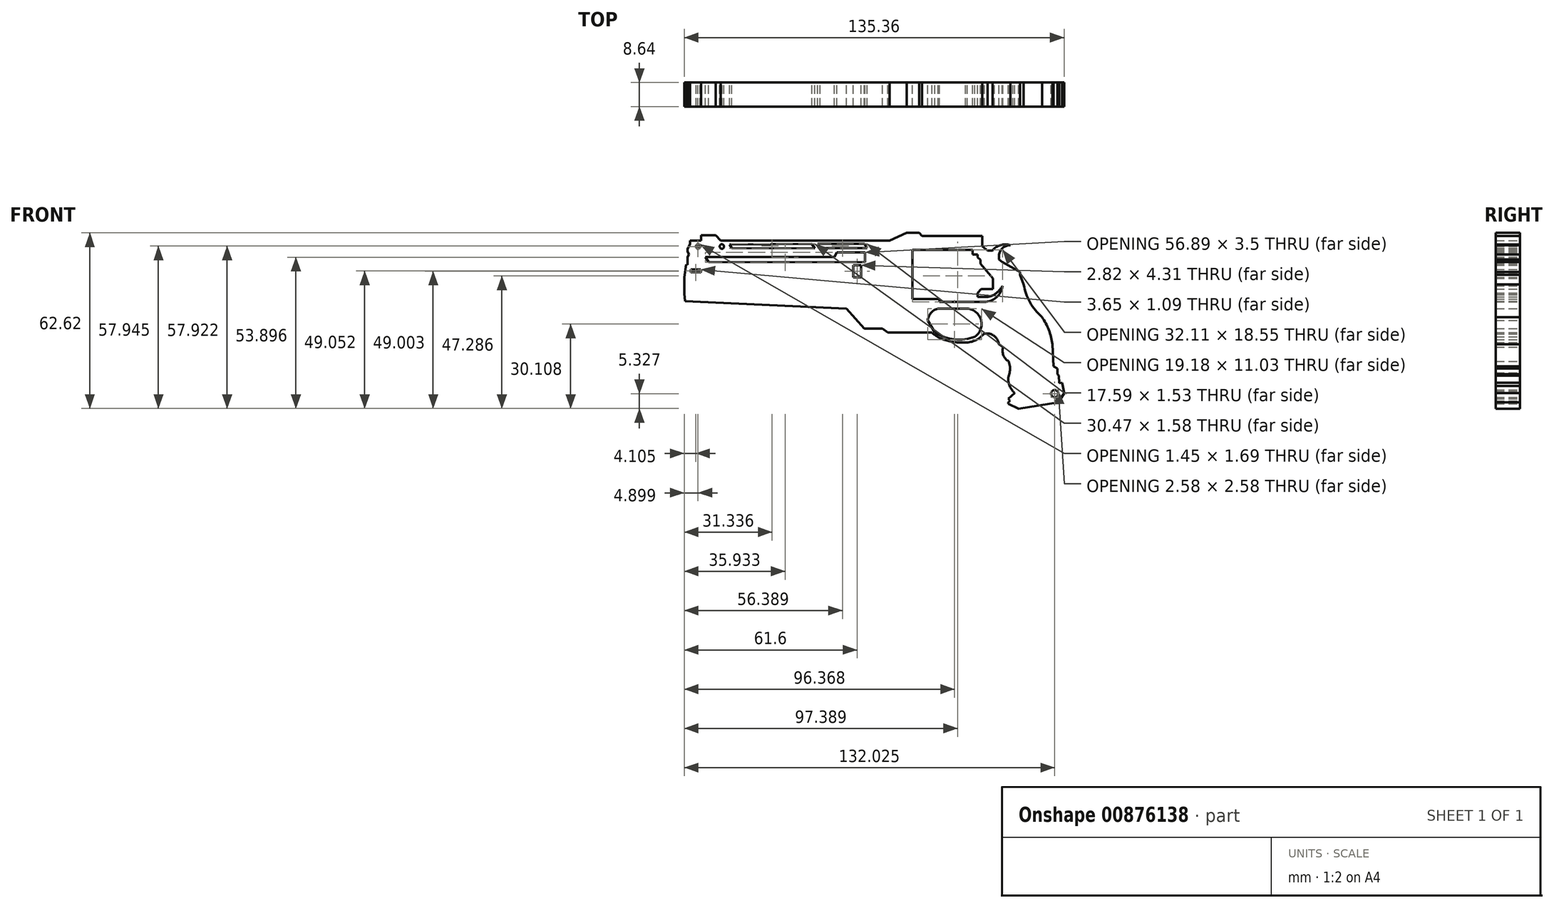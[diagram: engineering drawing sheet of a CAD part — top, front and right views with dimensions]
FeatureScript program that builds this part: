
annotation { "Feature Type Name" : "Feature", "Feature Type Description" : "" }
export const myFeature = defineFeature(function(context is Context, id is Id, definition is map)
    precondition{}
    {
        {
            var Q0;
            Q0=qCreatedBy(makeId("Front.planeOp"),FACE);
            var sketch = newSketch(context, id + "F0", { "sketchPlane" : qUnion([Q0])});
            skLineSegment(sketch, "E0", {"start": v(-67.89, 8.33) * mm, "end": v(-67.89, 14.23) * mm});
            skLineSegment(sketch, "E1", {"start": v(-67.89, 14.23) * mm, "end": v(-67.27, 18.7) * mm});
            skLineSegment(sketch, "E2", {"start": v(-67.27, 18.7) * mm, "end": v(-66.73, 18.63) * mm});
            skLineSegment(sketch, "E3", {"start": v(-66.73, 18.63) * mm, "end": v(-66.73, 21.38) * mm});
            skLineSegment(sketch, "E4", {"start": v(-66.73, 21.38) * mm, "end": v(-66.2, 22.3) * mm});
            skLineSegment(sketch, "E5", {"start": v(-66.2, 22.3) * mm, "end": v(-66.73, 23.47) * mm});
            skLineSegment(sketch, "E6", {"start": v(-66.73, 23.47) * mm, "end": v(-66.73, 24.31) * mm});
            skLineSegment(sketch, "E7", {"start": v(-66.73, 24.31) * mm, "end": v(-65.84, 25.94) * mm});
            skLineSegment(sketch, "E8", {"start": v(-65.84, 25.94) * mm, "end": v(-65.84, 27.21) * mm});
            skLineSegment(sketch, "E9", {"start": v(-65.84, 27.21) * mm, "end": v(5.25, 27.21) * mm});
            skLineSegment(sketch, "E10", {"start": v(5.25, 27.21) * mm, "end": v(11.39, 30) * mm});
            skLineSegment(sketch, "E11", {"start": v(11.39, 30) * mm, "end": v(15.19, 30) * mm});
            skLineSegment(sketch, "E12", {"start": v(15.19, 30) * mm, "end": v(15.88, 30) * mm});
            skLineSegment(sketch, "E13", {"start": v(15.88, 30) * mm, "end": v(16.87, 28.96) * mm});
            skLineSegment(sketch, "E14", {"start": v(16.87, 28.96) * mm, "end": v(38.33, 28.96) * mm});
            skLineSegment(sketch, "E15", {"start": v(38.33, 28.96) * mm, "end": v(38.33, 19.68) * mm});
            skLineSegment(sketch, "E16", {"start": v(38.33, 19.68) * mm, "end": v(40.93, 18) * mm});
            skLineSegment(sketch, "E17", {"start": v(40.93, 18) * mm, "end": v(42.2, 18) * mm});
            skLineSegment(sketch, "E18", {"start": v(42.2, 18) * mm, "end": v(45.38, 19.68) * mm});
            skLineSegment(sketch, "E19", {"start": v(45.38, 19.68) * mm, "end": v(38.33, 25.17) * mm});
            skLineSegment(sketch, "E20", {"start": v(45.38, 19.68) * mm, "end": v(51.8, 16.04) * mm});
            skLineSegment(sketch, "E21", {"start": v(51.8, 16.04) * mm, "end": v(51.8, 15.12) * mm});
            skLineSegment(sketch, "E22", {"start": v(51.8, 15.12) * mm, "end": v(46.94, 15.12) * mm});
            skArc(sketch, "E23", {"start": v(46.94, 15.12) * mm, "mid": v(45.8, 16.55) * mm, "end": v(44.1, 17.21) * mm});
            skArc(sketch, "E24", {"start": v(42.64, 8) * mm, "mid": v(45.55, 11.1) * mm, "end": v(46.94, 15.12) * mm});
            skArc(sketch, "E25", {"start": v(39.02, 7.14) * mm, "mid": v(40.89, 7.34) * mm, "end": v(42.64, 8) * mm});
            skLineSegment(sketch, "E26", {"start": v(39.02, 7.14) * mm, "end": v(23.08, 7.14) * mm});
            skLineSegment(sketch, "E27", {"start": v(23.08, 7.14) * mm, "end": v(23.08, 5.4) * mm});
            skLineSegment(sketch, "E28", {"start": v(23.08, 5.4) * mm, "end": v(39.02, 5.4) * mm});
            skArc(sketch, "E29", {"start": v(39.02, 5.4) * mm, "mid": v(43.36, 7.02) * mm, "end": v(45.55, 11.1) * mm});
            skArc(sketch, "E30", {"start": v(22.56, 3) * mm, "mid": v(20.04, 1.48) * mm, "end": v(18.89, -1.23) * mm});
            skArc(sketch, "E31", {"start": v(35.67, -7.02) * mm, "mid": v(37.89, -1.05) * mm, "end": v(32.98, 3) * mm});
            skArc(sketch, "E32", {"start": v(21.47, -5.51) * mm, "mid": v(28.4, -7.94) * mm, "end": v(35.67, -7.02) * mm});
            skLineSegment(sketch, "E33", {"start": v(21.47, -5.51) * mm, "end": v(18.89, -1.23) * mm});
            skLineSegment(sketch, "E34", {"start": v(22.56, 3) * mm, "end": v(32.98, 3) * mm});
            skArc(sketch, "E35", {"start": v(32.33, -9.05) * mm, "mid": v(35.94, -8.28) * mm, "end": v(38.85, -6) * mm});
            skArc(sketch, "E36", {"start": v(24.52, -8) * mm, "mid": v(28.37, -8.94) * mm, "end": v(32.33, -9.05) * mm});
            skArc(sketch, "E37", {"start": v(18, -2.7) * mm, "mid": v(20.82, -5.9) * mm, "end": v(24.52, -8) * mm});
            skArc(sketch, "E38", {"start": v(44.24, -9.7) * mm, "mid": v(42.4, -6.6) * mm, "end": v(38.85, -6) * mm});
            skLineSegment(sketch, "E39", {"start": v(44.24, -9.7) * mm, "end": v(45.72, -10.7) * mm});
            skArc(sketch, "E40", {"start": v(45.72, -10.7) * mm, "mid": v(45.85, -13.6) * mm, "end": v(47.73, -15.8) * mm});
            skArc(sketch, "E41", {"start": v(48.08, -19.87) * mm, "mid": v(48.19, -17.8) * mm, "end": v(47.73, -15.8) * mm});
            skArc(sketch, "E42", {"start": v(48.08, -19.87) * mm, "mid": v(47.7, -23.34) * mm, "end": v(49.28, -26.44) * mm});
            skArc(sketch, "E43", {"start": v(49.28, -26.44) * mm, "mid": v(49.57, -26.8) * mm, "end": v(49.9, -27.11) * mm});
            skLineSegment(sketch, "E44", {"start": v(49.9, -27.11) * mm, "end": v(47.57, -29.1) * mm});
            skLineSegment(sketch, "E45", {"start": v(47.57, -29.1) * mm, "end": v(48.2, -29.84) * mm});
            skLineSegment(sketch, "E46", {"start": v(48.2, -29.84) * mm, "end": v(47.57, -30.38) * mm});
            skLineSegment(sketch, "E47", {"start": v(47.57, -30.38) * mm, "end": v(47.57, -30.87) * mm});
            skLineSegment(sketch, "E48", {"start": v(47.57, -30.87) * mm, "end": v(51.25, -32.62) * mm});
            skLineSegment(sketch, "E49", {"start": v(51.25, -32.62) * mm, "end": v(65.5, -30.38) * mm});
            skLineSegment(sketch, "E50", {"start": v(65.5, -30.38) * mm, "end": v(67.47, -27.11) * mm});
            skLineSegment(sketch, "E51", {"start": v(67.47, -27.11) * mm, "end": v(66.96, -24.58) * mm});
            skLineSegment(sketch, "E52", {"start": v(66.96, -24.58) * mm, "end": v(61.97, -25.57) * mm});
            skLineSegment(sketch, "E53", {"start": v(61.97, -25.57) * mm, "end": v(60.63, -27.68) * mm});
            skLineSegment(sketch, "E54", {"start": v(60.63, -27.68) * mm, "end": v(47.57, -30.38) * mm});
            skLineSegment(sketch, "E55", {"start": v(49.9, -27.11) * mm, "end": v(63.92, -23.25) * mm});
            skArc(sketch, "E56", {"start": v(53.08, 11.64) * mm, "mid": v(55.33, 5.26) * mm, "end": v(59.59, 0) * mm});
            skArc(sketch, "E57", {"start": v(63.3, -9.75) * mm, "mid": v(62.05, -4.64) * mm, "end": v(59.59, 0) * mm});
            skLineSegment(sketch, "E58", {"start": v(63.3, -9.75) * mm, "end": v(63.92, -23.25) * mm});
            skLineSegment(sketch, "E59", {"start": v(63.67, -17.63) * mm, "end": v(65.1, -18.36) * mm});
            skLineSegment(sketch, "E60", {"start": v(65.1, -18.36) * mm, "end": v(65.18, -20.34) * mm});
            skLineSegment(sketch, "E61", {"start": v(65.18, -20.34) * mm, "end": v(65.67, -20.82) * mm});
            skLineSegment(sketch, "E62", {"start": v(65.67, -20.82) * mm, "end": v(65.79, -23.5) * mm});
            skLineSegment(sketch, "E63", {"start": v(65.79, -23.5) * mm, "end": v(66.77, -23.46) * mm});
            skLineSegment(sketch, "E64", {"start": v(66.77, -23.46) * mm, "end": v(66.96, -24.58) * mm});
            skLineSegment(sketch, "E65", {"start": v(53.08, 11.64) * mm, "end": v(51.8, 15.12) * mm});
            skLineSegment(sketch, "E66", {"start": v(42.34, 0) * mm, "end": v(50.31, 8.3) * mm});
            skLineSegment(sketch, "E67", {"start": v(50.31, 8.3) * mm, "end": v(51.56, 13.38) * mm});
            skPoint(sketch, "E67.endSnap0", {"position": v(52.44, 13.38) * mm});
            skLineSegment(sketch, "E68", {"start": v(42.34, 0) * mm, "end": v(43.97, -1.57) * mm});
            skLineSegment(sketch, "E69", {"start": v(43.97, -1.57) * mm, "end": v(52.1, 6.9) * mm});
            skLineSegment(sketch, "E70", {"start": v(52.1, 6.9) * mm, "end": v(53.08, 11.64) * mm});
            skLineSegment(sketch, "E71", {"start": v(20.37, -5.51) * mm, "end": v(4.66, -5.51) * mm});
            skLineSegment(sketch, "E72", {"start": v(4.66, -5.51) * mm, "end": v(2.8, -4.12) * mm});
            skLineSegment(sketch, "E73", {"start": v(2.8, -4.12) * mm, "end": v(15, -4.12) * mm});
            skLineSegment(sketch, "E74", {"start": v(2.8, -4.12) * mm, "end": v(-3.73, -4.12) * mm});
            skLineSegment(sketch, "E75", {"start": v(-3.73, -4.12) * mm, "end": v(-10.07, 2.98) * mm});
            skLineSegment(sketch, "E76", {"start": v(-10.07, 2.98) * mm, "end": v(-67.6, 5.7) * mm});
            skLineSegment(sketch, "E77", {"start": v(-67.6, 5.7) * mm, "end": v(-67.89, 8.33) * mm});
            skLineSegment(sketch, "E78", {"start": v(-8.15, 8.33) * mm, "end": v(-67.89, 8.33) * mm});
            skLineSegment(sketch, "E79", {"start": v(-67.89, 14.23) * mm, "end": v(-7.7, 14.23) * mm});
            skLineSegment(sketch, "E80", {"start": v(-7.7, 14.23) * mm, "end": v(-7.7, 18.54) * mm});
            skLineSegment(sketch, "E81", {"start": v(-7.7, 18.54) * mm, "end": v(-66.73, 18.63) * mm});
            skLineSegment(sketch, "E82", {"start": v(-66.73, 21.38) * mm, "end": v(-14.4, 21.38) * mm});
            skLineSegment(sketch, "E83", {"start": v(-14.4, 21.38) * mm, "end": v(-13.48, 23.03) * mm});
            skLineSegment(sketch, "E84", {"start": v(-13.48, 23.03) * mm, "end": v(-3.51, 23.03) * mm});
            skLineSegment(sketch, "E85", {"start": v(-3.51, 23.03) * mm, "end": v(-3.51, 19.53) * mm});
            skLineSegment(sketch, "E86", {"start": v(-3.51, 19.53) * mm, "end": v(-59.21, 19.61) * mm});
            skLineSegment(sketch, "E87", {"start": v(-59.21, 19.61) * mm, "end": v(-60.4, 21.38) * mm});
            skLineSegment(sketch, "E88", {"start": v(7.79, 16.11) * mm, "end": v(7.79, 8.33) * mm});
            skLineSegment(sketch, "E89", {"start": v(15.1, 6.47) * mm, "end": v(23.08, 6.47) * mm});
            skLineSegment(sketch, "E90", {"start": v(15.1, 6.47) * mm, "end": v(13.45, 6.47) * mm});
            skLineSegment(sketch, "E91", {"start": v(13.45, 6.47) * mm, "end": v(13.45, 23.94) * mm});
            skLineSegment(sketch, "E92", {"start": v(13.45, 23.94) * mm, "end": v(34.92, 23.94) * mm});
            skLineSegment(sketch, "E93", {"start": v(34.92, 23.94) * mm, "end": v(34.92, 7.14) * mm});
            skLineSegment(sketch, "E94", {"start": v(34.92, 22.36) * mm, "end": v(36.64, 22.36) * mm});
            skLineSegment(sketch, "E95", {"start": v(36.64, 22.36) * mm, "end": v(36.64, 21.3) * mm});
            skLineSegment(sketch, "E96", {"start": v(36.64, 21.3) * mm, "end": v(37.66, 20.43) * mm});
            skLineSegment(sketch, "E97", {"start": v(37.66, 20.43) * mm, "end": v(37.66, 13.86) * mm});
            skLineSegment(sketch, "E98", {"start": v(37.66, 13.86) * mm, "end": v(42.07, 13.86) * mm});
            skLineSegment(sketch, "E99", {"start": v(42.07, 13.86) * mm, "end": v(42.07, 10) * mm});
            skLineSegment(sketch, "E100", {"start": v(42.07, 10) * mm, "end": v(37.93, 10) * mm});
            skLineSegment(sketch, "E101", {"start": v(37.93, 10) * mm, "end": v(36.64, 8.65) * mm});
            skLineSegment(sketch, "E102", {"start": v(36.64, 8.65) * mm, "end": v(36.64, 7.14) * mm});
            skLineSegment(sketch, "E103", {"start": v(11.2, 7.8) * mm, "end": v(11.18, 7.8) * mm});
            skLineSegment(sketch, "E104", {"start": v(-7.7, 14.23) * mm, "end": v(-7.7, 8.33) * mm});
            skLineSegment(sketch, "E105", {"start": v(-7.7, 8.33) * mm, "end": v(7.79, 8.33) * mm});
            skLineSegment(sketch, "E106", {"start": v(-7.7, 14.23) * mm, "end": v(4.44, 14.23) * mm});
            skLineSegment(sketch, "E107", {"start": v(4.23, 16.11) * mm, "end": v(4.44, 16.11) * mm});
            skLineSegment(sketch, "E108", {"start": v(-4.88, 14.23) * mm, "end": v(-4.88, 18.48) * mm});
            skLineSegment(sketch, "E109", {"start": v(-4.88, 18.48) * mm, "end": v(-7.7, 18.54) * mm});
            skLineSegment(sketch, "E110", {"start": v(7.79, 18.62) * mm, "end": v(-7.7, 18.54) * mm});
            skLineSegment(sketch, "E111", {"start": v(7.79, 18.62) * mm, "end": v(13.45, 18.62) * mm});
            skLineSegment(sketch, "E112", {"start": v(-3.51, 23.03) * mm, "end": v(2.61, 23.03) * mm});
            skLineSegment(sketch, "E113", {"start": v(2.61, 23.03) * mm, "end": v(3.29, 22.46) * mm});
            skLineSegment(sketch, "E114", {"start": v(3.29, 22.46) * mm, "end": v(10.44, 22.46) * mm});
            skLineSegment(sketch, "E115", {"start": v(10.44, 22.46) * mm, "end": v(11.86, 24.01) * mm});
            skLineSegment(sketch, "E116", {"start": v(11.86, 24.01) * mm, "end": v(13.45, 23.94) * mm});
            skLineSegment(sketch, "E117", {"start": v(37.66, 18.98) * mm, "end": v(42.07, 13.86) * mm});
            skLineSegment(sketch, "E118", {"start": v(37.66, 15.97) * mm, "end": v(39.87, 13.86) * mm});
            skLineSegment(sketch, "E119", {"start": v(13.45, 11.6) * mm, "end": v(34.92, 11.6) * mm});
            skLineSegment(sketch, "E120", {"start": v(13.45, 20.43) * mm, "end": v(34.92, 20.43) * mm});
            skLineSegment(sketch, "E121", {"start": v(-66.2, 22.3) * mm, "end": v(-17.8, 22.3) * mm});
            skLineSegment(sketch, "E122", {"start": v(-17.8, 22.3) * mm, "end": v(-17.18, 23.2) * mm});
            skLineSegment(sketch, "E123", {"start": v(-17.18, 23.2) * mm, "end": v(2.58, 23.2) * mm});
            skLineSegment(sketch, "E124", {"start": v(2.58, 23.2) * mm, "end": v(2.61, 23.03) * mm});
            skLineSegment(sketch, "E125", {"start": v(-20.3, 25.86) * mm, "end": v(-19.45, 24.56) * mm});
            skLineSegment(sketch, "E126", {"start": v(-19.45, 24.56) * mm, "end": v(-2.7, 24.56) * mm});
            skLineSegment(sketch, "E127", {"start": v(-2.7, 24.56) * mm, "end": v(-3.55, 26.1) * mm});
            skLineSegment(sketch, "E128", {"start": v(-3.55, 26.1) * mm, "end": v(-20.3, 26.1) * mm});
            skLineSegment(sketch, "E129", {"start": v(-20.3, 26.1) * mm, "end": v(-19.45, 24.56) * mm});
            skLineSegment(sketch, "E130", {"start": v(-51.79, 25.86) * mm, "end": v(-50.95, 24.56) * mm});
            skLineSegment(sketch, "E131", {"start": v(-50.95, 24.56) * mm, "end": v(-21.32, 24.51) * mm});
            skLineSegment(sketch, "E132", {"start": v(-21.32, 24.51) * mm, "end": v(-22.34, 26.1) * mm});
            skLineSegment(sketch, "E133", {"start": v(-22.34, 26.1) * mm, "end": v(-51.79, 25.86) * mm});
            skArc(sketch, "E134", {"start": v(-54.48, 26) * mm, "mid": v(-55.24, 25.1) * mm, "end": v(-54.38, 24.3) * mm});
            skArc(sketch, "E135", {"start": v(-54.38, 24.3) * mm, "mid": v(-53.74, 25.2) * mm, "end": v(-54.48, 26) * mm});
            skArc(sketch, "E136", {"start": v(-63.1, 26) * mm, "mid": v(-63.72, 25.13) * mm, "end": v(-63.04, 24.3) * mm});
            skArc(sketch, "E137", {"start": v(-63.04, 24.3) * mm, "mid": v(-62.27, 25.18) * mm, "end": v(-63.1, 26) * mm});
            skLineSegment(sketch, "E138", {"start": v(-65.6, 16.93) * mm, "end": v(-65.61, 15.9) * mm});
            skLineSegment(sketch, "E139", {"start": v(-65.61, 15.9) * mm, "end": v(-61.96, 15.89) * mm});
            skLineSegment(sketch, "E140", {"start": v(-61.96, 15.89) * mm, "end": v(-61.96, 16.98) * mm});
            skLineSegment(sketch, "E141", {"start": v(-61.96, 16.98) * mm, "end": v(-65.6, 16.93) * mm});
            skLineSegment(sketch, "E142", {"start": v(-5.98, 2.52) * mm, "end": v(-2.7, -1.89) * mm});
            skLineSegment(sketch, "E143", {"start": v(-2.7, -1.89) * mm, "end": v(7.75, -1.9) * mm});
            skLineSegment(sketch, "E144", {"start": v(7.75, -1.9) * mm, "end": v(4.44, 2.93) * mm});
            skLineSegment(sketch, "E145", {"start": v(4.44, 2.93) * mm, "end": v(-5.98, 2.94) * mm});
            skArc(sketch, "E146", {"start": v(64.2, -26) * mm, "mid": v(62.85, -27.3) * mm, "end": v(64.2, -28.58) * mm});
            skArc(sketch, "E147", {"start": v(64.2, -28.58) * mm, "mid": v(65.42, -27.3) * mm, "end": v(64.2, -26) * mm});
            skLineSegment(sketch, "E148", {"start": v(40.17, 23.75) * mm, "end": v(41.94, 23.75) * mm});
            skArc(sketch, "E149", {"start": v(48.34, 25.62) * mm, "mid": v(44.85, 25.66) * mm, "end": v(41.94, 23.75) * mm});
            skArc(sketch, "E150", {"start": v(48.34, 25.62) * mm, "mid": v(45.7, 24.73) * mm, "end": v(44.33, 22.3) * mm});
            skLineSegment(sketch, "E151", {"start": v(44.33, 22.3) * mm, "end": v(44.33, 20.5) * mm});
            skArc(sketch, "E152", {"start": v(32.45, -3.4) * mm, "mid": v(32.36, -0.9) * mm, "end": v(30.98, 1.2) * mm});
            skArc(sketch, "E153", {"start": v(30.69, -6.92) * mm, "mid": v(31.8, -5.27) * mm, "end": v(32.45, -3.4) * mm});
            skLineSegment(sketch, "E154", {"start": v(30.69, -6.92) * mm, "end": v(31.22, -7.45) * mm});
            skArc(sketch, "E155", {"start": v(31.22, -7.45) * mm, "mid": v(33.17, -5.38) * mm, "end": v(33.92, -2.63) * mm});
            skLineSegment(sketch, "E156", {"start": v(33.92, -2.63) * mm, "end": v(33.92, 2.85) * mm});
            skLineSegment(sketch, "E157", {"start": v(30.98, 1.2) * mm, "end": v(28.9, 3) * mm});
            skLineSegment(sketch, "E158", {"start": v(-61.93, 27.21) * mm, "end": v(-61.93, 29.16) * mm});
            skLineSegment(sketch, "E159", {"start": v(-61.93, 29.16) * mm, "end": v(-56.72, 29.16) * mm});
            skLineSegment(sketch, "E160", {"start": v(-56.72, 29.16) * mm, "end": v(-54.9, 27.21) * mm});
            skPoint(sketch, "E161.end.orphan", {"position": v(11.2, 12.57) * mm});
            skPoint(sketch, "E161.start.orphan", {"position": v(11.2, 11.93) * mm});
            skSolve(sketch);
        }
        {
            var Q0;
            Q0 = qSketchRegion(id + "F0", true);
            extrude(context, id + "F1", {"entities" : qUnion([Q0]), "depth" : 8.64 * mm, "offsetDistance" : 25.4 * mm});
        }
    });
